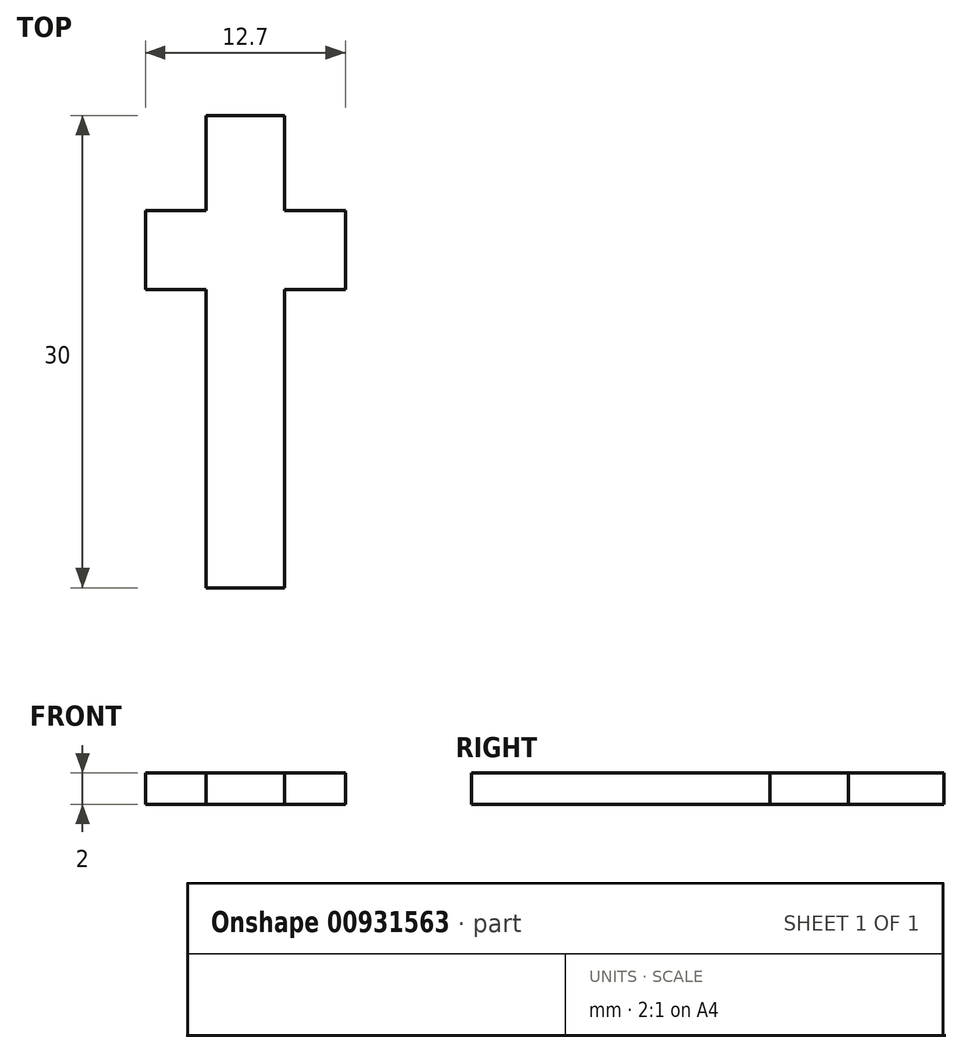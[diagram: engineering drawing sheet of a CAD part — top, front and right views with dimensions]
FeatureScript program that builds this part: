
annotation { "Feature Type Name" : "Feature", "Feature Type Description" : "" }
export const myFeature = defineFeature(function(context is Context, id is Id, definition is map)
    precondition{}
    {
        {
            var Q0;
            Q0=qCreatedBy(makeId("Top.planeOp"),FACE);
            var sketch = newSketch(context, id + "F0", { "sketchPlane" : qUnion([Q0])});
            skLineSegment(sketch, "E0", {"start": v(0, 13.95) * mm, "end": v(-2.5, 13.95) * mm});
            skLineSegment(sketch, "E1", {"start": v(-2.5, 13.95) * mm, "end": v(-2.5, 7.9) * mm});
            skLineSegment(sketch, "E2", {"start": v(-2.5, 7.9) * mm, "end": v(-6.35, 7.9) * mm});
            skLineSegment(sketch, "E3", {"start": v(-6.35, 7.9) * mm, "end": v(-6.35, 2.9) * mm});
            skLineSegment(sketch, "E4", {"start": v(-6.35, 2.9) * mm, "end": v(-2.5, 2.9) * mm});
            skLineSegment(sketch, "E5", {"start": v(-2.5, 2.9) * mm, "end": v(-2.5, -16.05) * mm});
            skLineSegment(sketch, "E6", {"start": v(-2.5, -16.05) * mm, "end": v(0, -16.05) * mm});
            skLineSegment(sketch, "E7", {"start": v(0, 13.95) * mm, "end": v(0, -16.05) * mm, "construction": true});
            skLineSegment(sketch, "E8.MirrorCS", {"start": v(0, 13.95) * mm, "end": v(2.5, 13.95) * mm});
            skLineSegment(sketch, "E9.MirrorCS", {"start": v(2.5, 13.95) * mm, "end": v(2.5, 7.9) * mm});
            skLineSegment(sketch, "E10.MirrorCS", {"start": v(2.5, 7.9) * mm, "end": v(6.35, 7.9) * mm});
            skLineSegment(sketch, "E11.MirrorCS", {"start": v(6.35, 7.9) * mm, "end": v(6.35, 2.9) * mm});
            skLineSegment(sketch, "E12.MirrorCS", {"start": v(6.35, 2.9) * mm, "end": v(2.5, 2.9) * mm});
            skLineSegment(sketch, "E13.MirrorCS", {"start": v(2.5, 2.9) * mm, "end": v(2.5, -16.05) * mm});
            skLineSegment(sketch, "E14.MirrorCS", {"start": v(2.5, -16.05) * mm, "end": v(0, -16.05) * mm});
            skSolve(sketch);
        }
        {
            var Q0;
            Q0=makeQuery(id+"F0.imprint","IMPRINT",FACE,{"disambiguationData":[TD([[makeQuery(id+"F0.imprint","IMPRINT",EDGE,{"derivedFrom":sQuery(id+"F0.wireOp",EDGE,"E0")}),1.0]])]});
            extrude(context, id + "F1", {"entities" : qUnion([Q0]), "depth" : 2 * mm, "offsetDistance" : 25 * mm});
        }
    });
